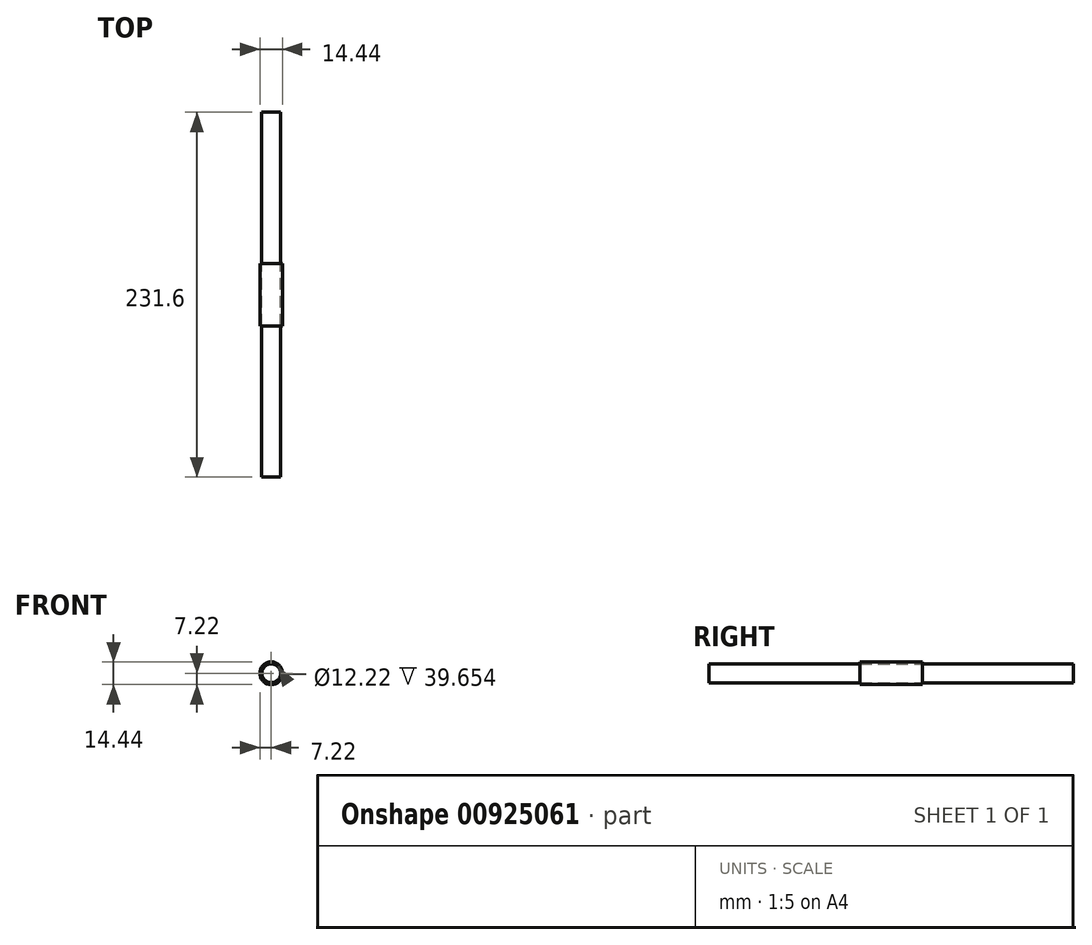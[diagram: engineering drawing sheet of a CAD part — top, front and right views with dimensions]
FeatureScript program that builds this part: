
annotation { "Feature Type Name" : "Feature", "Feature Type Description" : "" }
export const myFeature = defineFeature(function(context is Context, id is Id, definition is map)
    precondition{}
    {
        {
            var Q0;
            Q0=qCreatedBy(makeId("Front.planeOp"),FACE);
            var sketch = newSketch(context, id + "F0", { "sketchPlane" : qUnion([Q0])});
            skCircle(sketch, "E0", {"center": v(0, 0) * mm, "radius": 5.97 * mm});
            skSolve(sketch);
        }
        {
            var Q0;
            Q0 = qSketchRegion(id + "F0", true);
            extrude(context, id + "F1", {"entities" : qUnion([Q0]), "endBound" : BoundingType.SYMMETRIC, "depth" : 231.6 * mm, "offsetDistance" : 25.4 * mm});
        }
        {
            var Q0;
            Q0=qCreatedBy(makeId("Front.planeOp"),FACE);
            var sketch = newSketch(context, id + "F2", { "sketchPlane" : qUnion([Q0])});
            skCircle(sketch, "E1", {"center": v(0, 0) * mm, "radius": 6.1 * mm});
            skCircle(sketch, "E2.0", {"center": v(0, 0) * mm, "radius": 7.22 * mm});
            skSolve(sketch);
        }
        {
            var Q0;
            Q0=makeQuery(id+"F2.imprint","IMPRINT",FACE,{"disambiguationData":[TD([[makeQuery(id+"F2.imprint","IMPRINT",EDGE,{"derivedFrom":sQuery(id+"F2.wireOp",EDGE,"E1")}),-1.0]])]});
            extrude(context, id + "F3", {"entities" : qUnion([Q0]), "endBound" : BoundingType.SYMMETRIC, "depth" : 39.65 * mm, "offsetDistance" : 25.4 * mm});
        }
    });
